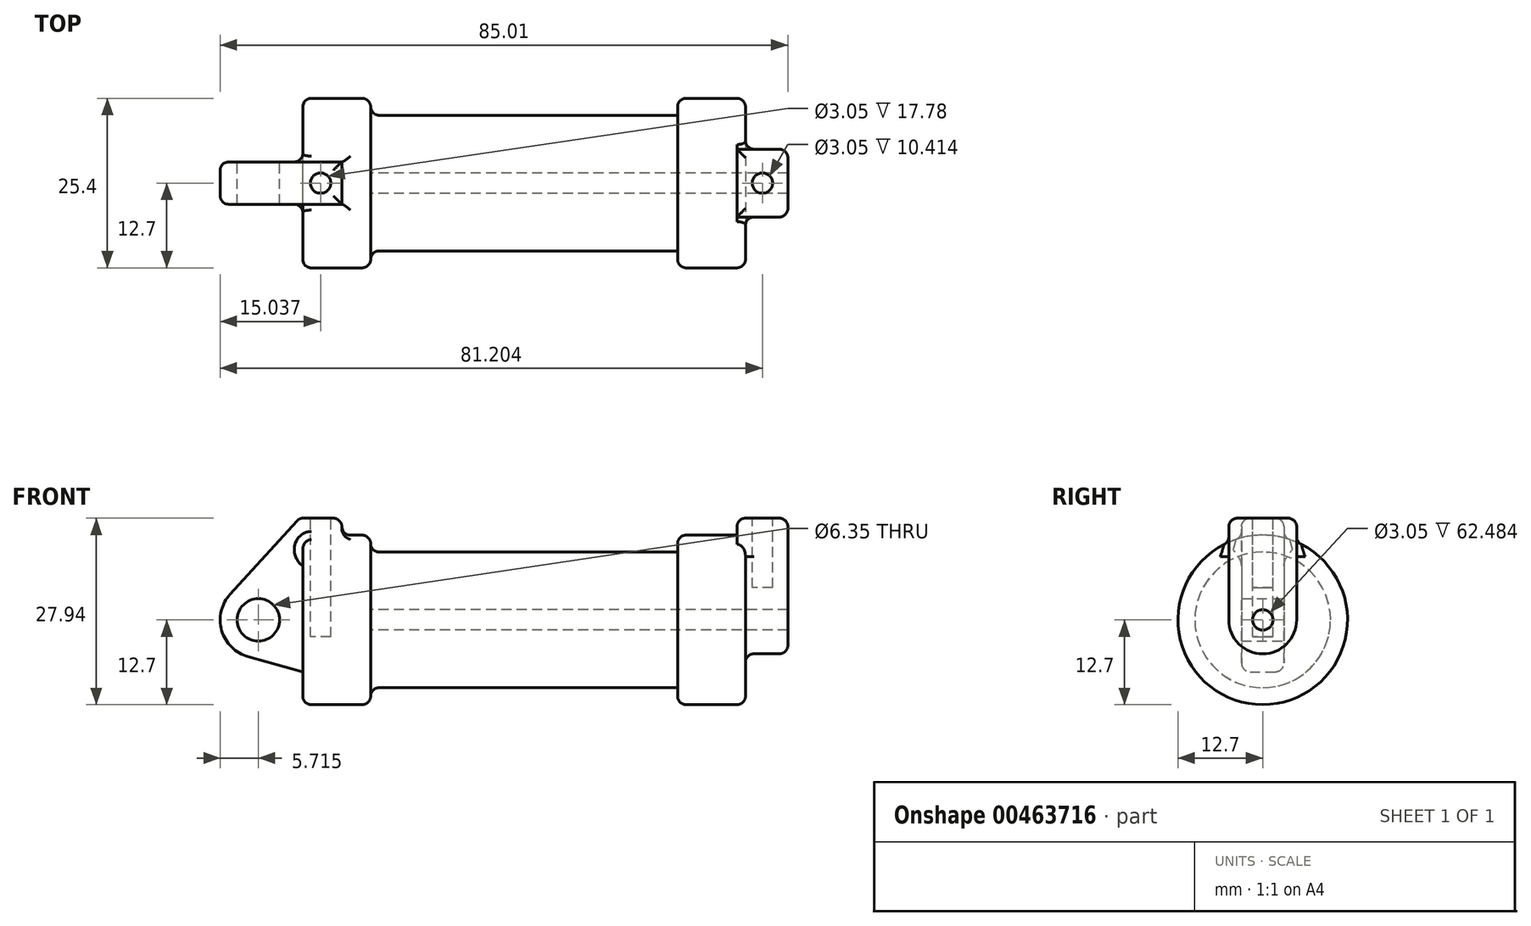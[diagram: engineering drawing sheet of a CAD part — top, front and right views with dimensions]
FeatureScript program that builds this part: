
annotation { "Feature Type Name" : "Feature", "Feature Type Description" : "" }
export const myFeature = defineFeature(function(context is Context, id is Id, definition is map)
    precondition{}
    {
        {
            var Q0;
            Q0=qCreatedBy(makeId("Front.planeOp"),FACE);
            var sketch = newSketch(context, id + "F0", { "sketchPlane" : qUnion([Q0])});
            skLineSegment(sketch, "E0", {"start": v(0, 0) * mm, "end": v(0, 12.7) * mm});
            skLineSegment(sketch, "E1", {"start": v(0, 12.7) * mm, "end": v(10.16, 12.7) * mm});
            skLineSegment(sketch, "E2", {"start": v(10.16, 12.7) * mm, "end": v(10.16, 10.16) * mm});
            skLineSegment(sketch, "E3", {"start": v(10.16, 10.16) * mm, "end": v(56.13, 10.16) * mm});
            skLineSegment(sketch, "E4", {"start": v(56.13, 10.16) * mm, "end": v(56.13, 12.7) * mm});
            skLineSegment(sketch, "E5", {"start": v(56.13, 12.7) * mm, "end": v(66.3, 12.7) * mm});
            skLineSegment(sketch, "E6", {"start": v(66.3, 12.7) * mm, "end": v(66.3, 0) * mm});
            skLineSegment(sketch, "E7", {"start": v(66.3, 0) * mm, "end": v(0, 0) * mm});
            skLineSegment(sketch, "E8", {"start": v(5.84, 15.24) * mm, "end": v(-0.5, 15.24) * mm});
            skLineSegment(sketch, "E9", {"start": v(-0.5, 15.24) * mm, "end": v(-10.88, 3.85) * mm});
            skLineSegment(sketch, "E10", {"start": v(0, 0) * mm, "end": v(-6.65, 0) * mm});
            skCircle(sketch, "E11", {"center": v(-6.65, 0) * mm, "radius": 5.72 * mm});
            skCircle(sketch, "E12", {"center": v(-6.65, 0) * mm, "radius": 3.18 * mm});
            skLineSegment(sketch, "E13", {"start": v(5.84, 15.24) * mm, "end": v(5.84, -9.4) * mm});
            skLineSegment(sketch, "E14", {"start": v(5.84, -9.4) * mm, "end": v(-8.18, -5.5) * mm});
            skSolve(sketch);
        }
        {
            var Q0;
            {var subQ0=sQuery(id+"F0.wireOp",EDGE,"E2");Q0=makeQuery(id+"F0.imprint","IMPRINT",FACE,{"disambiguationData":[TD([[makeQuery(id+"F0.imprint","IMPRINT",EDGE,{"derivedFrom":subQ0}),-1.0]])]});}
            var Q1;
            {var subQ0=sQuery(id+"F0.wireOp",EDGE,"E0");Q1=makeQuery(id+"F0.imprint","IMPRINT",FACE,{"disambiguationData":[TD([[makeQuery(id+"F0.imprint","IMPRINT",EDGE,{"derivedFrom":subQ0}),-1.0]])]});}
            var Q2;
            Q2=sQuery(id+"F0.wireOp",EDGE,"E7");
            revolve(context, id + "F1", {"entities" : qUnion([Q0, Q1]), "axis" : qUnion([Q2]), "revolveType" : RevolveType.FULL});
        }
        {
            var Q0;
            {var subQ1=sQuery(id+"F0.wireOp",EDGE,"E0");Q0=makeQuery(id+"F0.imprint","IMPRINT",FACE,{"disambiguationData":[TD([[makeQuery(id+"F0.imprint","IMPRINT",EDGE,{"derivedFrom":subQ1}),1.0]])]});}
            var Q1;
            {var subQ5=sQuery(id+"F0.wireOp",EDGE,"E12");Q1=makeQuery(id+"F0.imprint","IMPRINT",FACE,{"disambiguationData":[TD([[makeQuery(id+"F0.imprint","IMPRINT",EDGE,{"derivedFrom":subQ5}),-1.0]])]});}
            var Q2;
            {var subQ0=sQuery(id+"F0.wireOp",EDGE,"E0");Q2=makeQuery(id+"F0.imprint","IMPRINT",FACE,{"disambiguationData":[TD([[makeQuery(id+"F0.imprint","IMPRINT",EDGE,{"derivedFrom":subQ0}),-1.0]])]});}
            var Q3;
            {var subQ0=sQuery(id+"F0.wireOp",EDGE,"E14");Q3=makeQuery(id+"F0.imprint","IMPRINT",FACE,{"disambiguationData":[TD([[makeQuery(id+"F0.imprint","IMPRINT",EDGE,{"derivedFrom":subQ0}),-1.0]])]});}
            extrude(context, id + "F2", {"entities" : qUnion([Q0, Q1, Q2, Q3]), "operationType" : NewBodyOperationType.ADD, "endBound" : BoundingType.SYMMETRIC, "depth" : 6.35 * mm});
        }
        {
            var Q0;
            Q0=makeQuery(id+"F1.opRevolve","SWEPT_FACE",FACE,{"disambiguationData":[OSD([sQuery(id+"F0.wireOp",EDGE,"E6")])]});
            var sketch = newSketch(context, id + "F3", { "sketchPlane" : qUnion([Q0])});
            skCircle(sketch, "E15", {"center": v(0, 0) * mm, "radius": 1.52 * mm});
            skCircle(sketch, "E16", {"center": v(0, 0) * mm, "radius": 5.08 * mm});
            skLineSegment(sketch, "E17", {"start": v(-5.08, 0) * mm, "end": v(-5.08, 15.24) * mm});
            skLineSegment(sketch, "E18", {"start": v(5.08, 0) * mm, "end": v(5.08, 15.24) * mm});
            skLineSegment(sketch, "E19", {"start": v(5.08, 15.24) * mm, "end": v(-5.08, 15.24) * mm});
            skSolve(sketch);
        }
        {
            var Q0;
            {var subQ0=sQuery(id+"F3.wireOp",EDGE,"E19");Q0=makeQuery(id+"F3.imprint","IMPRINT",FACE,{"disambiguationData":[TD([[makeQuery(id+"F3.imprint","IMPRINT",EDGE,{"derivedFrom":subQ0}),1.0]])]});}
            extrude(context, id + "F4", {"entities" : qUnion([Q0]), "operationType" : NewBodyOperationType.ADD, "oppositeDirection" : true, "depth" : 1.27 * mm});
        }
        {
            var Q0;
            {var subQ0=sQuery(id+"F3.wireOp",EDGE,"E19");Q0=makeQuery(id+"F3.imprint","IMPRINT",FACE,{"disambiguationData":[TD([[makeQuery(id+"F3.imprint","IMPRINT",EDGE,{"derivedFrom":subQ0}),1.0]])]});}
            var Q1;
            {var subQ0=sQuery(id+"F3.wireOp",EDGE,"E17");var subQ1=sQuery(id+"F3.wireOp",EDGE,"E16");var subQ2=makeQuery(id+"F3.imprint","INTERSECT",VERTEX,{"derivedFrom":[subQ1,subQ0]});Q1=makeQuery(id+"F3.imprint","IMPRINT",FACE,{"disambiguationData":[TD([[makeQuery(id+"F3.imprint","IMPRINT",EDGE,{"disambiguationData":[TD([[subQ2,1.0]])],"derivedFrom":subQ1}),-1.0]])]});}
            var Q2;
            Q2=makeQuery(id+"F3.imprint","IMPRINT",FACE,{"disambiguationData":[TD([[makeQuery(id+"F3.imprint","IMPRINT",EDGE,{"derivedFrom":sQuery(id+"F3.wireOp",EDGE,"E15")}),-1.0]])]});
            extrude(context, id + "F5", {"entities" : qUnion([Q0, Q1, Q2]), "operationType" : NewBodyOperationType.ADD, "depth" : 6.35 * mm});
        }
        {
            var Q0;
            Q0=makeQuery(id+"F3.imprint","IMPRINT",FACE,{"disambiguationData":[TD([[makeQuery(id+"F3.imprint","IMPRINT",EDGE,{"derivedFrom":sQuery(id+"F3.wireOp",EDGE,"E15")}),1.0]])]});
            var Q1;
            Q1=makeQuery(id+"F1.opRevolve","SWEPT_FACE",FACE,{"disambiguationData":[OSD([sQuery(id+"F0.wireOp",EDGE,"E2")])]});
            extrude(context, id + "F6", {"entities" : qUnion([Q0]), "operationType" : NewBodyOperationType.REMOVE, "endBound" : BoundingType.UP_TO_SURFACE, "oppositeDirection" : true, "endBoundEntityFace" : qUnion([Q1]), "depth" : 25.4 * mm});
        }
        {
            var Q0;
            Q0=makeQuery(id+"F2.opExtrude","SWEPT_FACE",FACE,{"disambiguationData":[OSD([sQuery(id+"F0.wireOp",EDGE,"E8")])]});
            var sketch = newSketch(context, id + "F7", { "sketchPlane" : qUnion([Q0])});
            skCircle(sketch, "E20", {"center": v(2.67, 0) * mm, "radius": 1.52 * mm});
            skPoint(sketch, "E20.centerSnap0", {"position": v(2.67, 3.18) * mm});
            skPoint(sketch, "E20.centerSnap1", {"position": v(5.84, 0) * mm});
            skSolve(sketch);
        }
        {
            var Q0;
            {var subQ0=sQuery(id+"F3.wireOp",EDGE,"E19");Q0=makeQuery(id+"F5.boolean.opBoolean","MERGE",FACE,{"derivedFrom":[makeQuery(id+"F4.opExtrude","SWEPT_FACE",FACE,{"disambiguationData":[OSD([subQ0])]}),makeQuery(id+"F5.opExtrude","SWEPT_FACE",FACE,{"disambiguationData":[OSD([subQ0])]})]});}
            var sketch = newSketch(context, id + "F8", { "sketchPlane" : qUnion([Q0])});
            skCircle(sketch, "E21", {"center": v(68.83, 0) * mm, "radius": 1.52 * mm});
            skPoint(sketch, "E21.centerSnap0", {"position": v(68.83, 5.08) * mm});
            skPoint(sketch, "E21.centerSnap1", {"position": v(72.64, 0) * mm});
            skSolve(sketch);
        }
        {
            var Q0;
            Q0=makeQuery(id+"F7.imprint","IMPRINT",FACE,{"disambiguationData":[TD([[makeQuery(id+"F7.imprint","IMPRINT",EDGE,{"derivedFrom":sQuery(id+"F7.wireOp",EDGE,"E20")}),1.0]])]});
            extrude(context, id + "F9", {"entities" : qUnion([Q0]), "operationType" : NewBodyOperationType.REMOVE, "oppositeDirection" : true, "depth" : 17.78 * mm});
        }
        {
            var Q0;
            Q0=makeQuery(id+"F8.imprint","IMPRINT",FACE,{"disambiguationData":[TD([[makeQuery(id+"F8.imprint","IMPRINT",EDGE,{"derivedFrom":sQuery(id+"F8.wireOp",EDGE,"E21")}),1.0]])]});
            extrude(context, id + "F10", {"entities" : qUnion([Q0]), "operationType" : NewBodyOperationType.REMOVE, "oppositeDirection" : true, "depth" : 10.4 * mm});
        }
        {
            var Q0;
            Q0=makeQuery(id+"F5.opExtrude","CAP_EDGE",EDGE,{"disambiguationData":[OSD([sQuery(id+"F3.wireOp",EDGE,"E19")])],"isStart":false});
            var Q1;
            Q1=makeQuery(id+"F4.opExtrude","CAP_EDGE",EDGE,{"disambiguationData":[OSD([sQuery(id+"F3.wireOp",EDGE,"E19")])],"isStart":false});
            var Q2;
            {var subQ0=sQuery(id+"F3.wireOp",EDGE,"E19");var subQ1=sQuery(id+"F3.wireOp",EDGE,"E18");Q2=makeQuery(id+"F5.boolean.opBoolean","MERGE",EDGE,{"derivedFrom":[makeQuery(id+"F4.opExtrude","SWEPT_EDGE",EDGE,{"disambiguationData":[OSD([subQ1,subQ0])]}),makeQuery(id+"F5.opExtrude","SWEPT_EDGE",EDGE,{"disambiguationData":[OSD([subQ1,subQ0])]})]});}
            var Q3;
            {var subQ0=sQuery(id+"F3.wireOp",EDGE,"E19");var subQ1=sQuery(id+"F3.wireOp",EDGE,"E17");Q3=makeQuery(id+"F5.boolean.opBoolean","MERGE",EDGE,{"derivedFrom":[makeQuery(id+"F4.opExtrude","SWEPT_EDGE",EDGE,{"disambiguationData":[OSD([subQ1,subQ0])]}),makeQuery(id+"F5.opExtrude","SWEPT_EDGE",EDGE,{"disambiguationData":[OSD([subQ1,subQ0])]})]});}
            fillet(context, id + "F11", {"entities" : qUnion([Q0, Q1, Q2, Q3]), "radius" : 1.27 * mm, "tangentPropagation" : true, "allowEdgeOverflow" : false});
        }
        {
            var Q0;
            Q0=makeQuery(id+"F2.opExtrude","SWEPT_EDGE",EDGE,{"disambiguationData":[OSD([sQuery(id+"F0.wireOp",EDGE,"E8"),sQuery(id+"F0.wireOp",EDGE,"E13")])]});
            var Q1;
            Q1=makeQuery(id+"F2.opExtrude","CAP_EDGE",EDGE,{"disambiguationData":[OSD([sQuery(id+"F0.wireOp",EDGE,"E8")])],"isStart":true});
            var Q2;
            Q2=makeQuery(id+"F2.opExtrude","CAP_EDGE",EDGE,{"disambiguationData":[OSD([sQuery(id+"F0.wireOp",EDGE,"E8")])],"isStart":false});
            var Q3;
            Q3=makeQuery(id+"F2.opExtrude","SWEPT_EDGE",EDGE,{"disambiguationData":[OSD([sQuery(id+"F0.wireOp",EDGE,"E8"),sQuery(id+"F0.wireOp",EDGE,"E9")])]});
            var Q4;
            Q4=makeQuery(id+"F2.opExtrude","CAP_EDGE",EDGE,{"disambiguationData":[OSD([sQuery(id+"F0.wireOp",EDGE,"E9")])],"isStart":true});
            var Q5;
            Q5=makeQuery(id+"F2.opExtrude","CAP_EDGE",EDGE,{"disambiguationData":[OSD([sQuery(id+"F0.wireOp",EDGE,"E9")])],"isStart":false});
            fillet(context, id + "F12", {"entities" : qUnion([Q0, Q1, Q2, Q3, Q4, Q5]), "radius" : 1.27 * mm, "tangentPropagation" : true, "allowEdgeOverflow" : false});
        }
        {
            var Q0;
            Q0=makeQuery(id+"F1.opRevolve","SWEPT_EDGE",EDGE,{"disambiguationData":[OSD([sQuery(id+"F0.wireOp",EDGE,"E4"),sQuery(id+"F0.wireOp",EDGE,"E5")])]});
            var Q1;
            Q1=makeQuery(id+"F1.opRevolve","SWEPT_EDGE",EDGE,{"disambiguationData":[OSD([sQuery(id+"F0.wireOp",EDGE,"E5"),sQuery(id+"F0.wireOp",EDGE,"E6")])]});
            fillet(context, id + "F13", {"entities" : qUnion([Q0, Q1]), "radius" : 1.27 * mm, "tangentPropagation" : true, "allowEdgeOverflow" : false});
        }
        {
            var Q0;
            Q0=makeQuery(id+"F5.opExtrude","CAP_EDGE",EDGE,{"disambiguationData":[OSD([sQuery(id+"F3.wireOp",EDGE,"E18")])],"isStart":true});
            var Q1;
            Q1=makeQuery(id+"F5.opExtrude","CAP_EDGE",EDGE,{"disambiguationData":[OSD([sQuery(id+"F3.wireOp",EDGE,"E17")])],"isStart":true});
            var Q2;
            {var subQ0=sQuery(id+"F3.wireOp",EDGE,"E17");Q2=makeQuery(id+"F13.opFillet","BLEND_EDGE",EDGE,{"blendedFrom":[makeQuery(id+"F1.opRevolve","SWEPT_EDGE",EDGE,{"disambiguationData":[OSD([sQuery(id+"F0.wireOp",EDGE,"E5"),sQuery(id+"F0.wireOp",EDGE,"E6")])]}),makeQuery(id+"F5.boolean.opBoolean","MERGE",FACE,{"derivedFrom":[makeQuery(id+"F4.opExtrude","SWEPT_FACE",FACE,{"disambiguationData":[OSD([subQ0])]}),makeQuery(id+"F5.opExtrude","SWEPT_FACE",FACE,{"disambiguationData":[OSD([subQ0])]})]})],"blendedInto":[makeQuery(id+"F5.boolean.opBoolean","MERGE",FACE,{"derivedFrom":[makeQuery(id+"F4.opExtrude","SWEPT_FACE",FACE,{"disambiguationData":[OSD([subQ0])]}),makeQuery(id+"F5.opExtrude","SWEPT_FACE",FACE,{"disambiguationData":[OSD([subQ0])]})]})]});}
            var Q3;
            {var subQ0=sQuery(id+"F3.wireOp",EDGE,"E18");Q3=makeQuery(id+"F13.opFillet","BLEND_EDGE",EDGE,{"blendedFrom":[makeQuery(id+"F1.opRevolve","SWEPT_EDGE",EDGE,{"disambiguationData":[OSD([sQuery(id+"F0.wireOp",EDGE,"E5"),sQuery(id+"F0.wireOp",EDGE,"E6")])]}),makeQuery(id+"F5.boolean.opBoolean","MERGE",FACE,{"derivedFrom":[makeQuery(id+"F4.opExtrude","SWEPT_FACE",FACE,{"disambiguationData":[OSD([subQ0])]}),makeQuery(id+"F5.opExtrude","SWEPT_FACE",FACE,{"disambiguationData":[OSD([subQ0])]})]})],"blendedInto":[makeQuery(id+"F5.boolean.opBoolean","MERGE",FACE,{"derivedFrom":[makeQuery(id+"F4.opExtrude","SWEPT_FACE",FACE,{"disambiguationData":[OSD([subQ0])]}),makeQuery(id+"F5.opExtrude","SWEPT_FACE",FACE,{"disambiguationData":[OSD([subQ0])]})]})]});}
            fillet(context, id + "F14", {"entities" : qUnion([Q0, Q1, Q2, Q3]), "radius" : 1.27 * mm, "tangentPropagation" : true, "allowEdgeOverflow" : false});
        }
        {
            var Q0;
            Q0=makeQuery(id+"F5.opExtrude","CAP_EDGE",EDGE,{"disambiguationData":[OSD([sQuery(id+"F3.wireOp",EDGE,"E17")])],"isStart":false});
            var Q1;
            Q1=makeQuery(id+"F5.opExtrude","CAP_EDGE",EDGE,{"disambiguationData":[OSD([sQuery(id+"F3.wireOp",EDGE,"E18")])],"isStart":false});
            fillet(context, id + "F15", {"entities" : qUnion([Q0, Q1]), "radius" : 1.27 * mm, "tangentPropagation" : true, "allowEdgeOverflow" : false});
        }
        {
            var Q0;
            Q0=makeQuery(id+"F1.opRevolve","SWEPT_EDGE",EDGE,{"disambiguationData":[OSD([sQuery(id+"F0.wireOp",EDGE,"E2"),sQuery(id+"F0.wireOp",EDGE,"E3")])]});
            var Q1;
            Q1=makeQuery(id+"F1.opRevolve","SWEPT_EDGE",EDGE,{"disambiguationData":[OSD([sQuery(id+"F0.wireOp",EDGE,"E1"),sQuery(id+"F0.wireOp",EDGE,"E2")])]});
            var Q2;
            Q2=makeQuery(id+"F1.opRevolve","SWEPT_EDGE",EDGE,{"disambiguationData":[OSD([sQuery(id+"F0.wireOp",EDGE,"E0"),sQuery(id+"F0.wireOp",EDGE,"E1")])]});
            var Q3;
            Q3=makeQuery(id+"F2.boolean.opBoolean","INTERSECT",EDGE,{"derivedFrom":[makeQuery(id+"F1.opRevolve","SWEPT_FACE",FACE,{"disambiguationData":[OSD([sQuery(id+"F0.wireOp",EDGE,"E1")])]}),makeQuery(id+"F2.opExtrude","CAP_FACE",FACE,{"disambiguationData":[OSD([sQuery(id+"F0.wireOp",EDGE,"E8"),sQuery(id+"F0.wireOp",EDGE,"E9"),sQuery(id+"F0.wireOp",EDGE,"E11"),sQuery(id+"F0.wireOp",EDGE,"E12"),sQuery(id+"F0.wireOp",EDGE,"E13"),sQuery(id+"F0.wireOp",EDGE,"E14")])],"isStart":false})]});
            var Q4;
            Q4=makeQuery(id+"F2.boolean.opBoolean","INTERSECT",EDGE,{"derivedFrom":[makeQuery(id+"F1.opRevolve","SWEPT_FACE",FACE,{"disambiguationData":[OSD([sQuery(id+"F0.wireOp",EDGE,"E1")])]}),makeQuery(id+"F2.opExtrude","SWEPT_FACE",FACE,{"disambiguationData":[OSD([sQuery(id+"F0.wireOp",EDGE,"E13")])]})]});
            var Q5;
            Q5=makeQuery(id+"F2.boolean.opBoolean","INTERSECT",EDGE,{"derivedFrom":[makeQuery(id+"F1.opRevolve","SWEPT_FACE",FACE,{"disambiguationData":[OSD([sQuery(id+"F0.wireOp",EDGE,"E1")])]}),makeQuery(id+"F2.opExtrude","CAP_FACE",FACE,{"disambiguationData":[OSD([sQuery(id+"F0.wireOp",EDGE,"E8"),sQuery(id+"F0.wireOp",EDGE,"E9"),sQuery(id+"F0.wireOp",EDGE,"E11"),sQuery(id+"F0.wireOp",EDGE,"E12"),sQuery(id+"F0.wireOp",EDGE,"E13"),sQuery(id+"F0.wireOp",EDGE,"E14")])],"isStart":true})]});
            fillet(context, id + "F16", {"entities" : qUnion([Q0, Q1, Q2, Q3, Q4, Q5]), "radius" : 1.27 * mm, "tangentPropagation" : true, "allowEdgeOverflow" : false});
        }
    });
